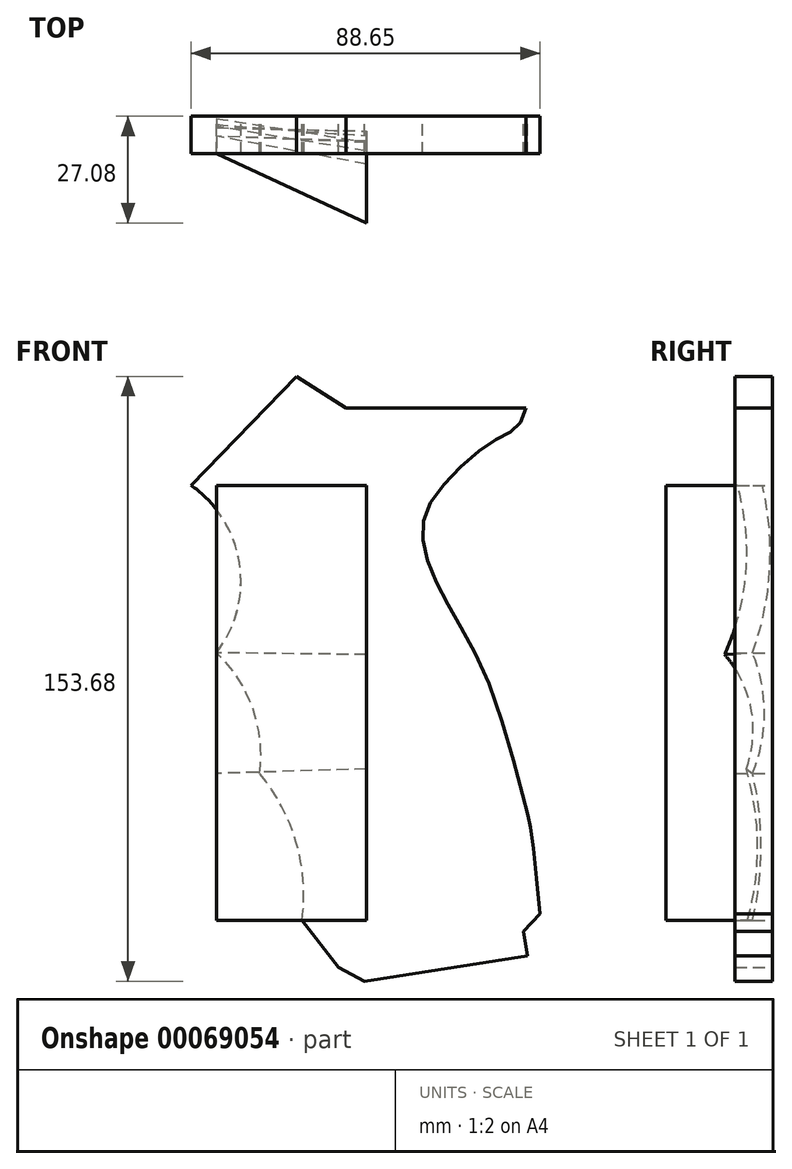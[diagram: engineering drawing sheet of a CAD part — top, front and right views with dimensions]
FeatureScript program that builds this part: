
annotation { "Feature Type Name" : "Feature", "Feature Type Description" : "" }
export const myFeature = defineFeature(function(context is Context, id is Id, definition is map)
    precondition{}
    {
        {
            var Q0;
            Q0=qCreatedBy(makeId("Front.planeOp"),FACE);
            var sketch = newSketch(context, id + "F0", { "sketchPlane" : qUnion([Q0])});
            skLineSegment(sketch, "E0", {"start": v(-20.17, 2.84) * mm, "end": v(25.55, 2.84) * mm});
            skLineSegment(sketch, "E1", {"start": v(-20.17, 2.84) * mm, "end": v(-32.68, 10.88) * mm});
            skLineSegment(sketch, "E2", {"start": v(-32.68, 10.88) * mm, "end": v(-59.5, -16.79) * mm});
            skArc(sketch, "E3", {"start": v(-53, -59.36) * mm, "mid": v(-47.16, -36.69) * mm, "end": v(-59.5, -16.79) * mm});
            skArc(sketch, "E4", {"start": v(-42.05, -90.01) * mm, "mid": v(-43.82, -73.36) * mm, "end": v(-53, -59.36) * mm});
            skArc(sketch, "E5", {"start": v(-31.24, -127.32) * mm, "mid": v(-32.76, -107.54) * mm, "end": v(-42.05, -90.01) * mm});
            skLineSegment(sketch, "E6", {"start": v(-31.24, -127.32) * mm, "end": v(-21.98, -139.23) * mm});
            skLineSegment(sketch, "E7", {"start": v(-21.98, -139.23) * mm, "end": v(-15.36, -142.8) * mm});
            skLineSegment(sketch, "E8", {"start": v(-15.36, -142.8) * mm, "end": v(25.93, -136.37) * mm});
            skLineSegment(sketch, "E9", {"start": v(25.93, -136.37) * mm, "end": v(24.95, -130.08) * mm});
            skLineSegment(sketch, "E10", {"start": v(24.95, -130.08) * mm, "end": v(29.15, -125.64) * mm});
            skFitSpline(sketch, "E11", {"points": [v(29.15, -125.64) * mm, v(26.81, -103.83) * mm, v(25.74, -99.41) * mm, v(16.37, -67.68) * mm, v(5.89, -47.33) * mm, v(0, -33.88) * mm, v(0, -24.25) * mm, v(7.16, -14.03) * mm, v(17.68, -5.3) * mm, v(23.1, -2.3) * mm, v(25.55, 2.84) * mm], "startDerivative": vector(-19.9, 209.85) * mm, "endDerivative": vector(28.25, 89.47) * mm});
            skSolve(sketch);
        }
        {
            var Q0;
            Q0=makeQuery(id+"F0.imprint","IMPRINT",FACE,{"disambiguationData":[TD([[makeQuery(id+"F0.imprint","IMPRINT",EDGE,{"derivedFrom":sQuery(id+"F0.wireOp",EDGE,"E0")}),-1.0]])]});
            extrude(context, id + "F1", {"entities" : qUnion([Q0]), "depth" : 9.52 * mm});
        }
        {
            var Q0;
            Q0=makeQuery(id+"F1.opExtrude","SWEPT_EDGE",EDGE,{"disambiguationData":[OSD([sQuery(id+"F0.wireOp",EDGE,"E3"),sQuery(id+"F0.wireOp",EDGE,"E4")])]});
            cPlane(context, id + "F2", {"entities" : qUnion([Q0]), "cplaneType" : CPlaneType.LINE_ANGLE, "offset" : 25.4 * mm, "angle" : 90 * degree, "width" : 152.4 * mm, "height" : 152.4 * mm});
        }
        {
            var Q0;
            Q0=qCreatedBy(id+"F2.planeOp",FACE);
            var sketch = newSketch(context, id + "F3", { "sketchPlane" : qUnion([Q0])});
            skLineSegment(sketch, "E12.0", {"start": v(-9.53, -16.79) * mm, "end": v(0, -16.79) * mm});
            skArc(sketch, "E13", {"start": v(-5.08, -59.36) * mm, "mid": v(-0.7, -38.26) * mm, "end": v(-2.54, -16.79) * mm});
            skLineSegment(sketch, "E14", {"start": v(0, -16.79) * mm, "end": v(0, -59.36) * mm});
            skLineSegment(sketch, "E15.0", {"start": v(0, -90.01) * mm, "end": v(0, -59.36) * mm});
            skLineSegment(sketch, "E16.0", {"start": v(0, -127.32) * mm, "end": v(0, -90.01) * mm});
            skArc(sketch, "E17", {"start": v(-5.08, -90.01) * mm, "mid": v(-2.05, -74.68) * mm, "end": v(-5.08, -59.36) * mm});
            skArc(sketch, "E18", {"start": v(-5.08, -127.32) * mm, "mid": v(-2.88, -108.66) * mm, "end": v(-5.08, -90.01) * mm});
            skLineSegment(sketch, "E19", {"start": v(-5.08, -127.32) * mm, "end": v(0, -127.32) * mm});
            skLineSegment(sketch, "E20", {"start": v(-5.08, -127.32) * mm, "end": v(-9.53, -127.32) * mm});
            skLineSegment(sketch, "E21", {"start": v(-9.53, -127.32) * mm, "end": v(-9.53, -16.79) * mm});
            skSolve(sketch);
        }
        {
            var Q0;
            Q0=qCreatedBy(id+"F2.planeOp",FACE);
            cPlane(context, id + "F4", {"entities" : qUnion([Q0]), "cplaneType" : CPlaneType.OFFSET, "offset" : 38.1 * mm, "width" : 152.4 * mm, "height" : 152.4 * mm});
        }
        {
            var Q0;
            Q0=qCreatedBy(id+"F4.planeOp",FACE);
            var sketch = newSketch(context, id + "F5", { "sketchPlane" : qUnion([Q0])});
            skPoint(sketch, "E22.0", {"position": v(-0.7, -38.26) * mm});
            skLineSegment(sketch, "E23.0", {"start": v(0, -16.79) * mm, "end": v(0, -59.36) * mm});
            skLineSegment(sketch, "E24", {"start": v(0, -16.79) * mm, "end": v(-8.9, -16.79) * mm});
            skArc(sketch, "E25.0", {"start": v(-12.15, -59.81) * mm, "mid": v(-6.72, -38.6) * mm, "end": v(-8.9, -16.79) * mm});
            skArc(sketch, "E26.0", {"start": v(-6.68, -88.89) * mm, "mid": v(-5.4, -73.6) * mm, "end": v(-12.15, -59.81) * mm});
            skArc(sketch, "E27.0", {"start": v(-6.35, -127.32) * mm, "mid": v(-3.77, -108.08) * mm, "end": v(-6.68, -88.89) * mm});
            skLineSegment(sketch, "E28.0", {"start": v(0, -127.32) * mm, "end": v(0, -90.01) * mm});
            skLineSegment(sketch, "E29.0", {"start": v(0, -90.01) * mm, "end": v(0, -59.36) * mm});
            skLineSegment(sketch, "E30", {"start": v(0, -127.32) * mm, "end": v(-6.35, -127.32) * mm});
            skLineSegment(sketch, "E31", {"start": v(-8.9, -16.79) * mm, "end": v(-27.08, -16.79) * mm});
            skLineSegment(sketch, "E32", {"start": v(-27.08, -16.79) * mm, "end": v(-27.08, -127.32) * mm});
            skLineSegment(sketch, "E33", {"start": v(-27.08, -127.32) * mm, "end": v(-6.35, -127.32) * mm});
            skSolve(sketch);
        }
        {
            var Q0;
            Q0=makeQuery(id+"F5.imprint","IMPRINT",FACE,{"disambiguationData":[TD([[makeQuery(id+"F5.imprint","IMPRINT",EDGE,{"derivedFrom":sQuery(id+"F5.wireOp",EDGE,"E25.0")}),1.0]])]});
            var Q1;
            Q1=makeQuery(id+"F3.imprint","IMPRINT",FACE,{"disambiguationData":[TD([[makeQuery(id+"F3.imprint","IMPRINT",EDGE,{"derivedFrom":sQuery(id+"F3.wireOp",EDGE,"E13")}),1.0]])]});
            loft(context, id + "F6", {"sheetProfilesArray" : [{ "sheetProfileEntities" : qUnion([Q0]) }, { "sheetProfileEntities" : qUnion([Q1]) }]});
        }
    });
